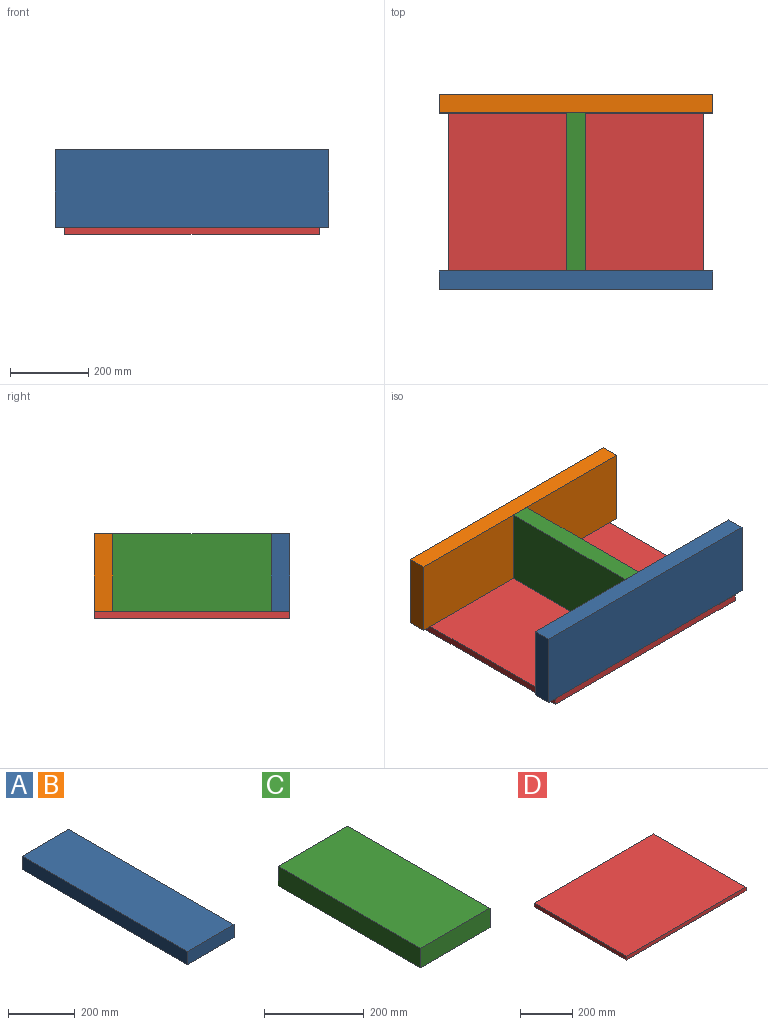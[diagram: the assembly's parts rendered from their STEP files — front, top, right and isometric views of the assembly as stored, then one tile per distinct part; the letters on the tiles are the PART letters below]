
ASSEMBLY  parts=4 mates=3
PART A: 6 faces, bbox 198x700x48 mm
  f0: plane 700x198mm, normal (0,0,1), area 138600mm2, adj f1,f3,f4,f5
  f1: plane 700x48mm, normal (-1,0,0), area 33600mm2, adj f0,f2,f4,f5
  f2: plane 700x198mm, normal (0,0,-1), area 138600mm2, adj f1,f3,f4,f5
  f3: plane 700x48mm, normal (1,0,0), area 33600mm2, adj f0,f2,f4,f5
  f4: plane 198x48mm, normal (0,-1,0), area 9504mm2, adj f0,f1,f2,f3
  f5: plane 198x48mm, normal (0,1,0), area 9504mm2, adj f0,f1,f2,f3
PART B: same geometry as A
PART C: 6 faces, bbox 198x404x48 mm
  f0: plane 404x198mm, normal (0,0,1), area 79992mm2, adj f1,f3,f4,f5
  f1: plane 404x48mm, normal (-1,0,0), area 19392mm2, adj f0,f2,f4,f5
  f2: plane 404x198mm, normal (0,0,-1), area 79992mm2, adj f1,f3,f4,f5
  f3: plane 404x48mm, normal (1,0,0), area 19392mm2, adj f0,f2,f4,f5
  f4: plane 198x48mm, normal (0,-1,0), area 9504mm2, adj f0,f1,f2,f3
  f5: plane 198x48mm, normal (0,1,0), area 9504mm2, adj f0,f1,f2,f3
PART D: 6 faces, bbox 650x500x18 mm
  f0: plane 650x18mm, normal (0,1,0), area 11700mm2, adj f1,f3,f4,f5
  f1: plane 500x18mm, normal (-1,0,0), area 9000mm2, adj f0,f2,f4,f5
  f2: plane 650x18mm, normal (0,-1,0), area 11700mm2, adj f1,f3,f4,f5
  f3: plane 500x18mm, normal (1,0,0), area 9000mm2, adj f0,f2,f4,f5
  f4: plane 650x500mm, normal (0,0,1), area 325000mm2, adj f0,f1,f2,f3
  f5: plane 650x500mm, normal (0,0,-1), area 325000mm2, adj f0,f1,f2,f3
PLACE A rot(axis=(-0.58,0.58,0.58),120deg) t=(-430.05,-31.05,117.7)mm
PLACE B rot(axis=(-0.58,0.58,0.58),120deg) t=(-430.05,420.95,117.7)mm
PLACE C rot(axis=(0.71,0,-0.71),180deg) t=(-80.05,-7.05,117.7)mm
PLACE D t=(-80.05,194.95,0.7)mm
MATE fastened C.f5 <-> A.f0  axis (0,-1,0) through (-80.05,-7.05,117.7)mm
MATE fastened A.f3 <-> D.f4  axis (0,0,-1) through (-80.05,-31.05,18.7)mm
MATE fastened B.f3 <-> D.f4  axis (0,0,-1) through (-80.05,420.95,18.7)mm
